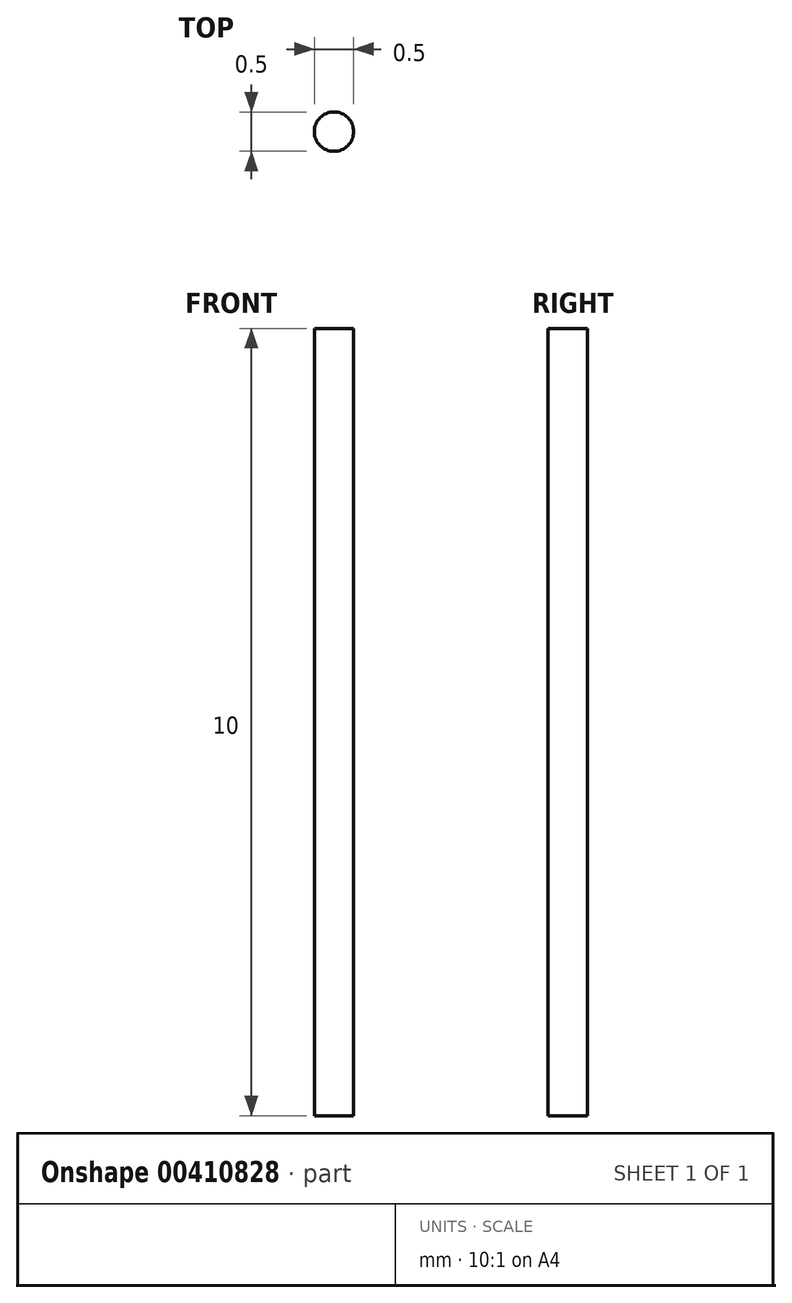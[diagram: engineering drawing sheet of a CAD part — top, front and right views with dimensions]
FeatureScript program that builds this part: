
annotation { "Feature Type Name" : "Feature", "Feature Type Description" : "" }
export const myFeature = defineFeature(function(context is Context, id is Id, definition is map)
    precondition{}
    {
        {
            var Q0;
            Q0=qCreatedBy(makeId("Top.planeOp"),FACE);
            var sketch = newSketch(context, id + "F0", { "sketchPlane" : qUnion([Q0])});
            skCircle(sketch, "E0", {"center": v(0, 0) * mm, "radius": 0.25 * mm});
            skSolve(sketch);
        }
        {
            var Q0;
            Q0 = qSketchRegion(id + "F0", true);
            extrude(context, id + "F1", {"entities" : qUnion([Q0]), "depth" : 10 * mm});
        }
    });
